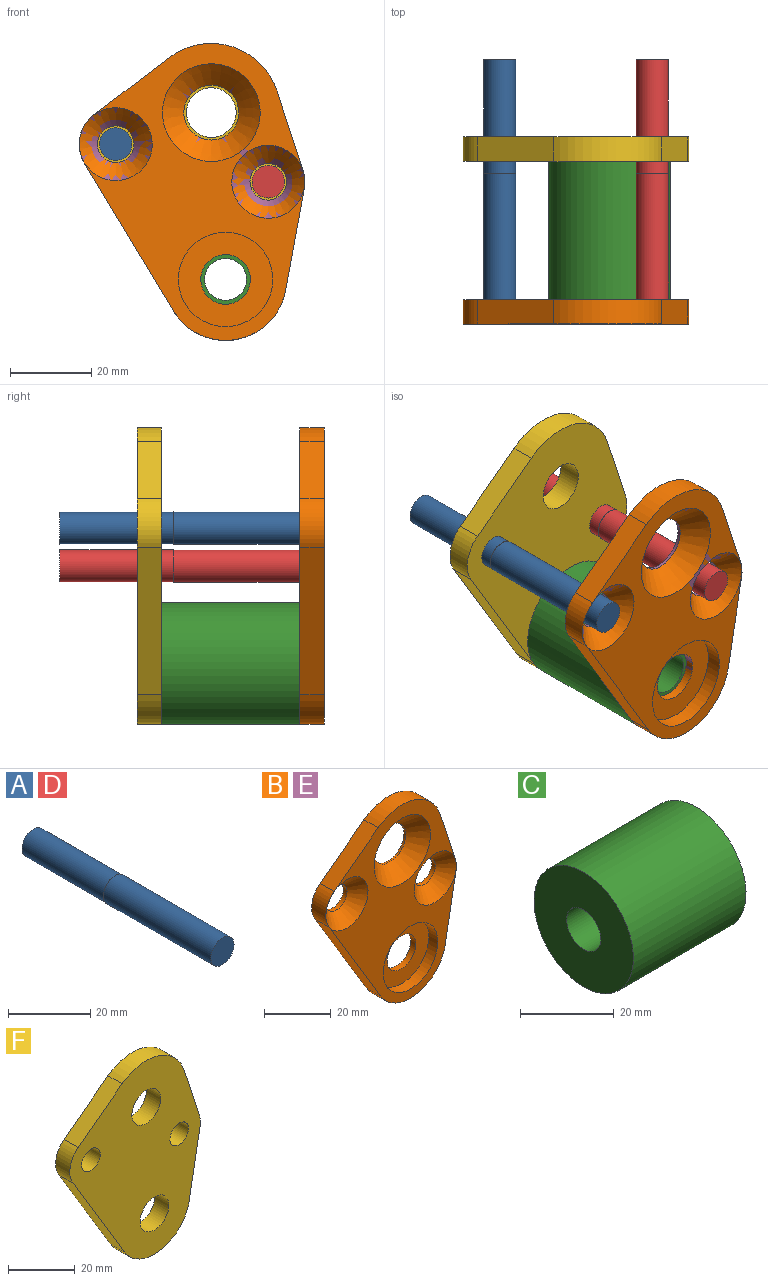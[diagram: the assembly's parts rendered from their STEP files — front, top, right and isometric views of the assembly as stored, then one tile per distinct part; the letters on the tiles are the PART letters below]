
ASSEMBLY  parts=6 mates=4
PART A: 5 faces, bbox 8x65x8 mm
  f0: cylinder r=4mm len=37mm, axis (0,-1,0), area 929.9mm2, adj f1,f2
  f1: plane 8x8mm, normal (0,1,0), area 2.5mm2, adj f0,f3
  f2: plane 8x8mm, normal (0,-1,0), area 50.3mm2, adj f0
  f3: cylinder r=3.9mm len=28mm, axis (0,-1,0), area 686.1mm2, adj f1,f4
  f4: plane 7.8x7.8mm, normal (0,1,0), area 47.8mm2, adj f3
PART B: 19 faces, bbox 55.5x6x73 mm
  f0: plane 36.33x21.86mm, normal (-0.86,0,-0.52), area 254.4mm2, adj f1,f7,f8,f9
  f1: cylinder r=15mm len=27.61mm, axis (0,-1,0), area 217.7mm2, adj f0,f2,f8,f9
  f2: plane 25.08x6mm, normal (0.98,0,-0.18), area 153mm2, adj f1,f3,f8,f9
  f3: cylinder r=9mm len=6mm, axis (0,-1,0), area 26.9mm2, adj f2,f4,f8,f9
  f4: plane 19.5x6.4mm, normal (0.95,0,0.31), area 123.1mm2, adj f3,f5,f8,f9
  f5: cylinder r=17mm len=26.42mm, axis (0,-1,0), area 194mm2, adj f4,f6,f8,f9
  f6: plane 18.67x14.14mm, normal (-0.6,0,0.8), area 140.5mm2, adj f5,f7,f8,f9
  f7: cylinder r=9mm len=11.81mm, axis (0,-1,0), area 79.1mm2, adj f0,f6,f8,f9
  f8: plane 73x55.5mm, normal (0,1,0), area 2377.7mm2, adj f0,f1,f2,f3,f4,f5,f6,f7
  f9: plane 73x55.5mm, normal (0,-1,0), area 1385.4mm2, adj f0,f1,f2,f3,f4,f5,f6,f7
  f10: cylinder r=6.1mm len=12.2mm, axis (0,-1,0), area 84.3mm2, adj f8,f11
  f11: plane 23.2x23.2mm, normal (0,-1,0), area 305.8mm2, adj f10,f12
  f12: cylinder r=11.6mm len=23.2mm, axis (0,-1,0), area 277mm2, adj f9,f11
  f13: cylinder r=6.75mm len=13.5mm, axis (0,-1,0), area 31.8mm2, adj f8,f14
  f14: cone r=6.75mm half-angle=45deg, axis (0,-1,0), area 437.3mm2, adj f9,f13
  f15: cylinder r=4.5mm len=9mm, axis (0,-1,0), area 43.5mm2, adj f8,f16
  f16: cone r=4.5mm half-angle=45deg, axis (0,-1,0), area 266.7mm2, adj f9,f15
  f17: cylinder r=4.5mm len=9mm, axis (0,-1,0), area 43.5mm2, adj f8,f18
  f18: cone r=4.5mm half-angle=45deg, axis (0,-1,0), area 266.7mm2, adj f9,f17
PART C: 4 faces, bbox 34x30x30 mm
  f0: cylinder r=15mm len=34mm, axis (1,0,0), area 3204.4mm2, adj f1,f2
  f1: plane 30x30mm, normal (-1,0,0), area 623.5mm2, adj f0,f3
  f2: plane 30x30mm, normal (1,0,0), area 623.5mm2, adj f0,f3
  f3: cylinder r=5.15mm len=34mm, axis (1,0,0), area 1100.2mm2, adj f1,f2
PART D: same geometry as A
PART E: same geometry as B
PART F: 14 faces, bbox 55.5x6x73 mm
  f0: plane 36.33x21.86mm, normal (-0.86,0,-0.52), area 254.4mm2, adj f1,f7,f8,f9
  f1: cylinder r=15mm len=27.61mm, axis (0,-1,0), area 217.7mm2, adj f0,f2,f8,f9
  f2: plane 25.08x6mm, normal (0.98,0,-0.18), area 153mm2, adj f1,f3,f8,f9
  f3: cylinder r=9mm len=6mm, axis (0,-1,0), area 26.9mm2, adj f2,f4,f8,f9
  f4: plane 19.5x6.4mm, normal (0.95,0,0.31), area 123.1mm2, adj f3,f5,f8,f9
  f5: cylinder r=17mm len=26.42mm, axis (0,-1,0), area 194mm2, adj f4,f6,f8,f9
  f6: plane 18.67x14.14mm, normal (-0.6,0,0.8), area 140.5mm2, adj f5,f7,f8,f9
  f7: cylinder r=9mm len=11.81mm, axis (0,-1,0), area 79.1mm2, adj f0,f6,f8,f9
  f8: plane 73x55.5mm, normal (0,1,0), area 2433.2mm2, adj f0,f1,f2,f3,f4,f5,f6,f7
  f9: plane 73x55.5mm, normal (0,-1,0), area 2433.2mm2, adj f0,f1,f2,f3,f4,f5,f6,f7
  f10: cylinder r=6.1mm len=12.2mm, axis (0,-1,0), area 230mm2, adj f8,f9
  f11: cylinder r=6.1mm len=12.2mm, axis (0,-1,0), area 230mm2, adj f8,f9
  f12: cylinder r=3.95mm len=7.9mm, axis (0,-1,0), area 148.9mm2, adj f8,f9
  f13: cylinder r=3.95mm len=7.9mm, axis (0,-1,0), area 148.9mm2, adj f8,f9
PLACE A t=(-41.15,-1.08,29.91)mm
PLACE B t=(-14.15,-1.08,-3.33)mm fixed
PLACE C rot(axis=(0,0,-1),90deg) t=(-14.15,4.92,-3.33)mm
PLACE D t=(-3.65,-1.08,20.67)mm
PLACE E t=(-14.15,-1.08,-3.33)mm
PLACE F t=(-14.15,38.92,-3.33)mm
MATE fastened C.f0 <-> B.f10  axis (0,-1,0) through (-14.15,4.92,-3.33)mm
MATE fastened D.f0 <-> B.f3  axis (0,-1,0) through (-3.65,-1.08,20.67)mm
MATE fastened F.f1 <-> C.f0  axis (0,-1,0) through (-14.15,38.92,-3.33)mm
MATE fastened A.f0 <-> B.f7  axis (0,-1,0) through (-41.15,-1.08,29.91)mm
